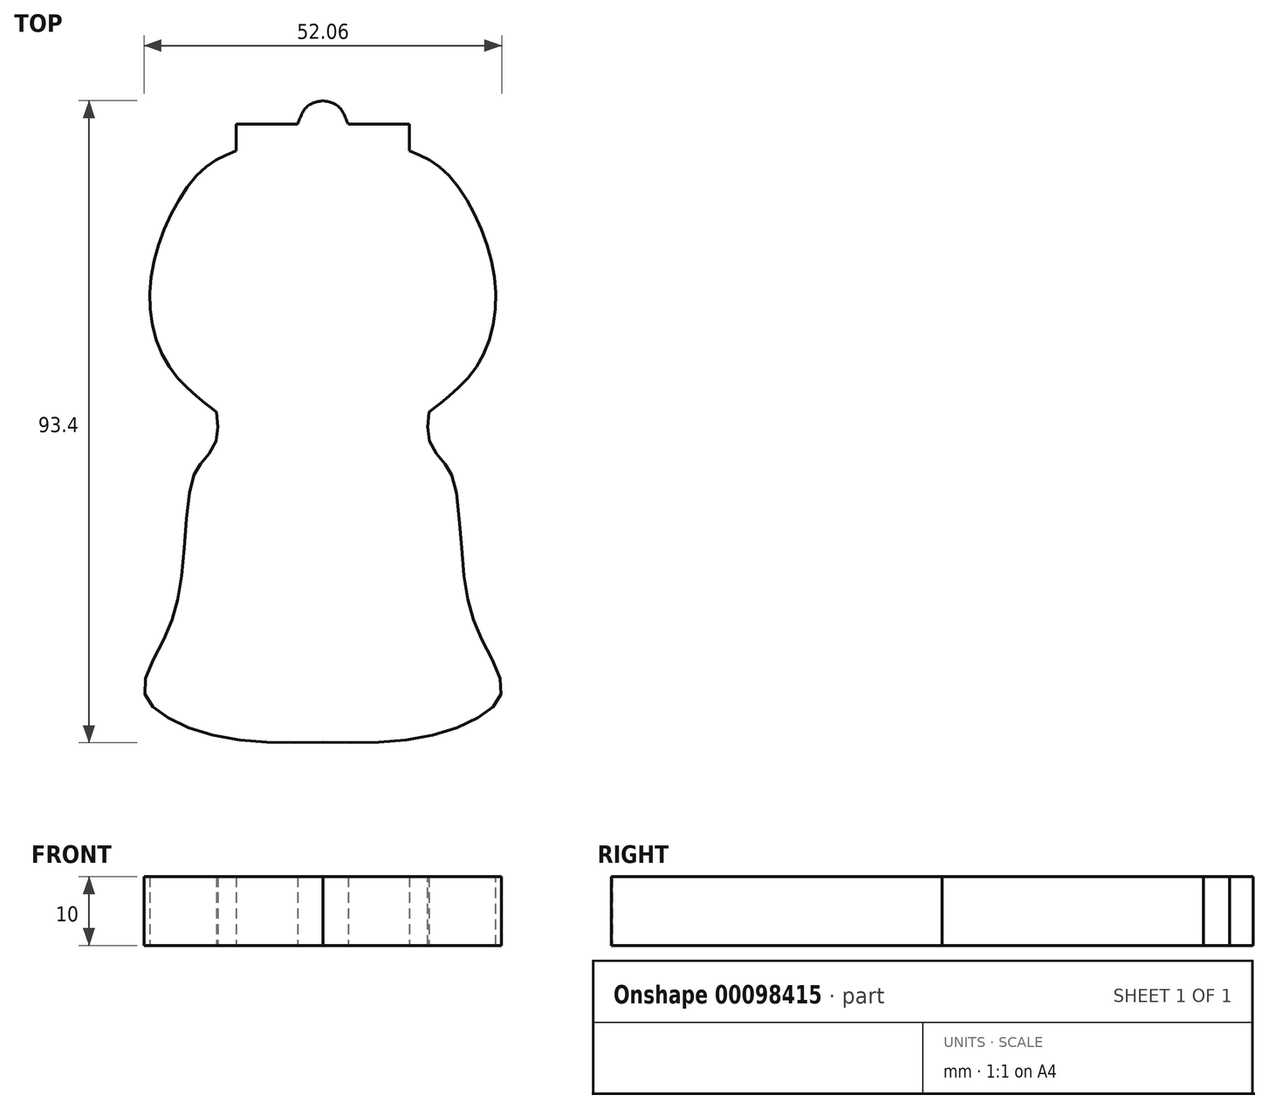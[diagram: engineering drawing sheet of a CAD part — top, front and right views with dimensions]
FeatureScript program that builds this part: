
annotation { "Feature Type Name" : "Feature", "Feature Type Description" : "" }
export const myFeature = defineFeature(function(context is Context, id is Id, definition is map)
    precondition{}
    {
        {
            var Q0;
            Q0=qCreatedBy(makeId("Top.planeOp"),FACE);
            var sketch = newSketch(context, id + "F0", { "sketchPlane" : qUnion([Q0])});
            skFitSpline(sketch, "E0", {"points": [v(0, 56.88) * mm, v(-2.2, 56.1) * mm, v(-3.68, 53.44) * mm], "startDerivative": vector(-5.17, -0.9) * mm, "endDerivative": vector(-2.25, -5.86) * mm});
            skLineSegment(sketch, "E1", {"start": v(-3.68, 53.44) * mm, "end": v(-12.62, 53.44) * mm});
            skLineSegment(sketch, "E2", {"start": v(-12.62, 53.44) * mm, "end": v(-12.62, 49.6) * mm});
            skFitSpline(sketch, "E3", {"points": [v(-12.62, 49.6) * mm, v(-17.49, 46.83) * mm, v(-22.86, 38.65) * mm, v(-25.2, 27.67) * mm, v(-22.4, 18.2) * mm, v(-17.49, 13.17) * mm, v(-15.44, 11.56) * mm], "startDerivative": vector(-33.15, -13.9) * mm, "endDerivative": vector(12.74, -8.27) * mm});
            skFitSpline(sketch, "E4", {"points": [v(-15.44, 11.56) * mm, v(-15.44, 7.6) * mm, v(-17.49, 4.4) * mm, v(-19.12, 1.37) * mm, v(-20.52, -11.95) * mm, v(-22.86, -20.95) * mm, v(-26.02, -28.31) * mm, v(-24.03, -31.94) * mm, v(-14.33, -35.8) * mm, v(0, -36.45) * mm], "startDerivative": vector(3.48, -52.43) * mm, "endDerivative": vector(94.66, 2.07) * mm});
            skLineSegment(sketch, "E5", {"start": v(0, 62.25) * mm, "end": v(0, -47.42) * mm, "construction": true});
            skLineSegment(sketch, "E6", {"start": v(0, -47.42) * mm, "end": v(0.95, -47.42) * mm, "construction": true});
            skLineSegment(sketch, "E7.MirrorCS", {"start": v(3.68, 53.44) * mm, "end": v(12.62, 53.44) * mm});
            skFitSpline(sketch, "E8.MirrorCS", {"points": [v(0, 56.88) * mm, v(2.2, 56.1) * mm, v(3.68, 53.44) * mm], "startDerivative": vector(5.17, -0.9) * mm, "endDerivative": vector(2.25, -5.86) * mm});
            skLineSegment(sketch, "E9.MirrorCS", {"start": v(12.62, 53.44) * mm, "end": v(12.62, 49.6) * mm});
            skFitSpline(sketch, "E10.MirrorCS", {"points": [v(12.62, 49.6) * mm, v(17.49, 46.83) * mm, v(22.86, 38.65) * mm, v(25.2, 27.67) * mm, v(22.4, 18.2) * mm, v(17.49, 13.17) * mm, v(15.44, 11.56) * mm], "startDerivative": vector(33.15, -13.9) * mm, "endDerivative": vector(-12.74, -8.27) * mm});
            skFitSpline(sketch, "E11.MirrorCS", {"points": [v(15.44, 11.56) * mm, v(15.44, 7.6) * mm, v(17.49, 4.4) * mm, v(19.12, 1.37) * mm, v(20.52, -11.95) * mm, v(22.86, -20.95) * mm, v(26.02, -28.31) * mm, v(24.03, -31.94) * mm, v(14.33, -35.8) * mm, v(0, -36.45) * mm], "startDerivative": vector(-3.48, -52.43) * mm, "endDerivative": vector(-94.66, 2.07) * mm});
            skSolve(sketch);
        }
        {
            var Q0;
            Q0 = qSketchRegion(id + "F0", true);
            extrude(context, id + "F1", {"entities" : qUnion([Q0]), "depth" : 10 * mm});
        }
    });
